# Revit family: Shower-Door-STERLING-DELUXE-5905_1
name_source: partatom
category: Specialty Equipment
revit_build: Autodesk Revit 2017 (Build: 20160225_1515(x64)
units: mm (PartAtom-declared; Revit-internal decimal feet)

## family parameters
Cut with Voids When Loaded = No
Host = Face
OmniClass Number = 23.31.17.17
OmniClass Title = Shower Enclosures
Part Type = Normal
Room Calculation Point = No
Round Connector Dimension = Use Diameter
Shared = No

## types (1)
- S-Silver
    ADA Compliant = No
    Assembly Code = C1030200
    Date Modified = 08/30/2021
    Default Elevation = 0"
    Description = Framed sliding bath door, 56-1/4 inch H x 52-3/4 - 57-3/4 inch W, with 1/8 inch thick Rain glass
    Finish = Sterling-Metal-S-Silver
    Height = 56 1/4"
    Length = 2 5/16"
    Manufacturer = STERLING Co.
    MasterFormat 2014 = 10 28 19.16
    MasterFormat 2014 Name = Shower Door
    Material = Premium Metal Construction
    Model = 5905-3G05-S
    Product Documentation Link = https://resources.kohler.com
    Product Name = Deluxe
    Product Page URL = http://www.sterlingplumbing.com
    Type = 1
    URL = https://www.sterlingplumbing.com
https://www.sterlingplumbing.com
    WaterSense Certified = No

## geometry (parser evidence)
native form markers: Sweep x5
no freeform markers — native parametric forms only
